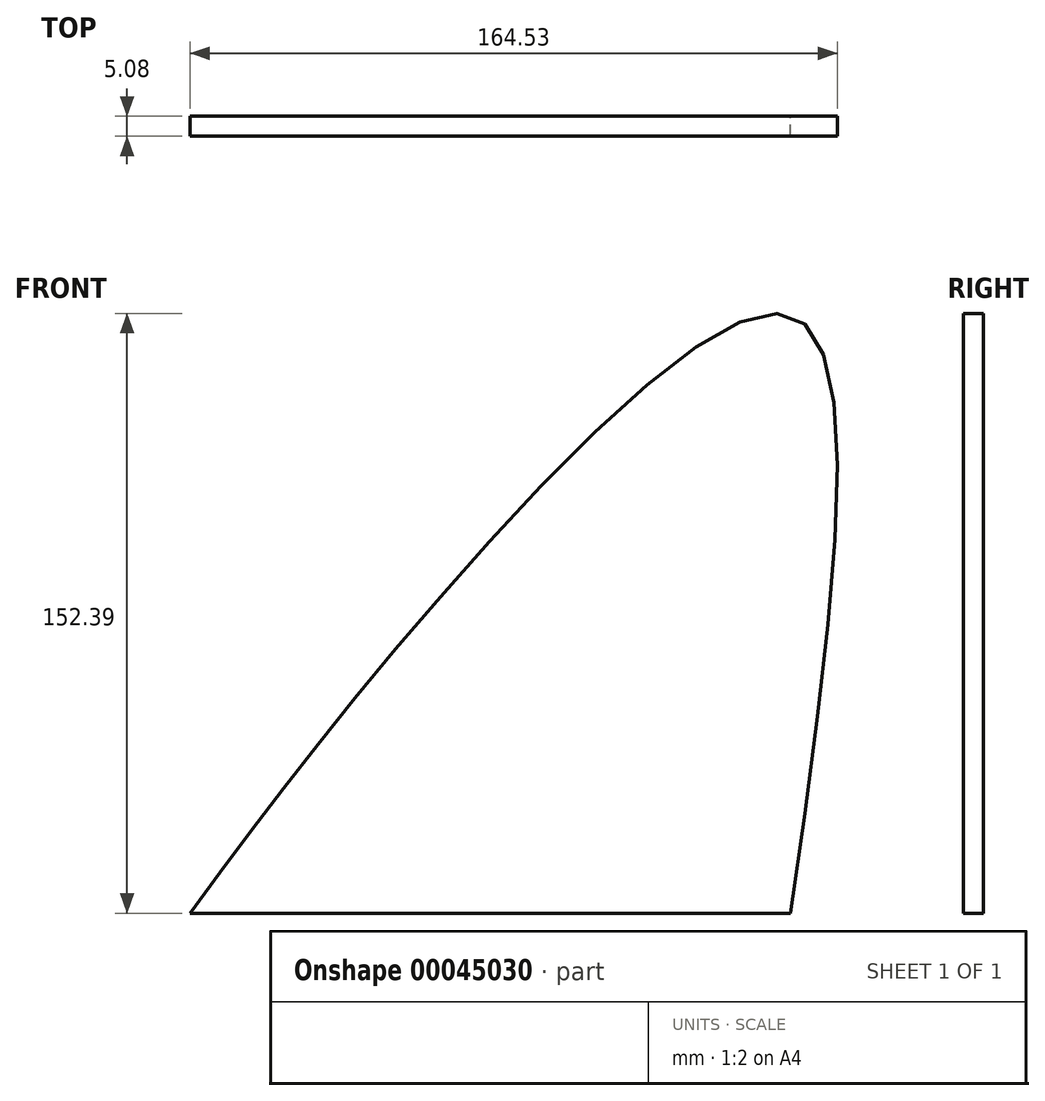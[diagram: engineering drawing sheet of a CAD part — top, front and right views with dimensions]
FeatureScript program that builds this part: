
annotation { "Feature Type Name" : "Feature", "Feature Type Description" : "" }
export const myFeature = defineFeature(function(context is Context, id is Id, definition is map)
    precondition{}
    {
        {
            var Q0;
            Q0=qCreatedBy(makeId("Front.planeOp"),FACE);
            var sketch = newSketch(context, id + "F0", { "sketchPlane" : qUnion([Q0])});
            skLineSegment(sketch, "E0", {"start": v(-75.7, -31.75) * mm, "end": v(76.92, -31.75) * mm});
            skFitSpline(sketch, "E1", {"points": [v(76.92, -31.75) * mm, v(76.92, 120.06) * mm, v(-11.2, 49.65) * mm, v(-75.7, -31.75) * mm], "startDerivative": vector(83.2, 584.15) * mm, "endDerivative": vector(-176.2, -238.52) * mm});
            skSolve(sketch);
        }
        {
            var Q0;
            Q0=makeQuery(id+"F0.imprint","IMPRINT",FACE,{"disambiguationData":[TD([[makeQuery(id+"F0.imprint","IMPRINT",EDGE,{"derivedFrom":sQuery(id+"F0.wireOp",EDGE,"E0")}),1.0]])]});
            extrude(context, id + "F1", {"entities" : qUnion([Q0]), "depth" : 5.08 * mm});
        }
    });
